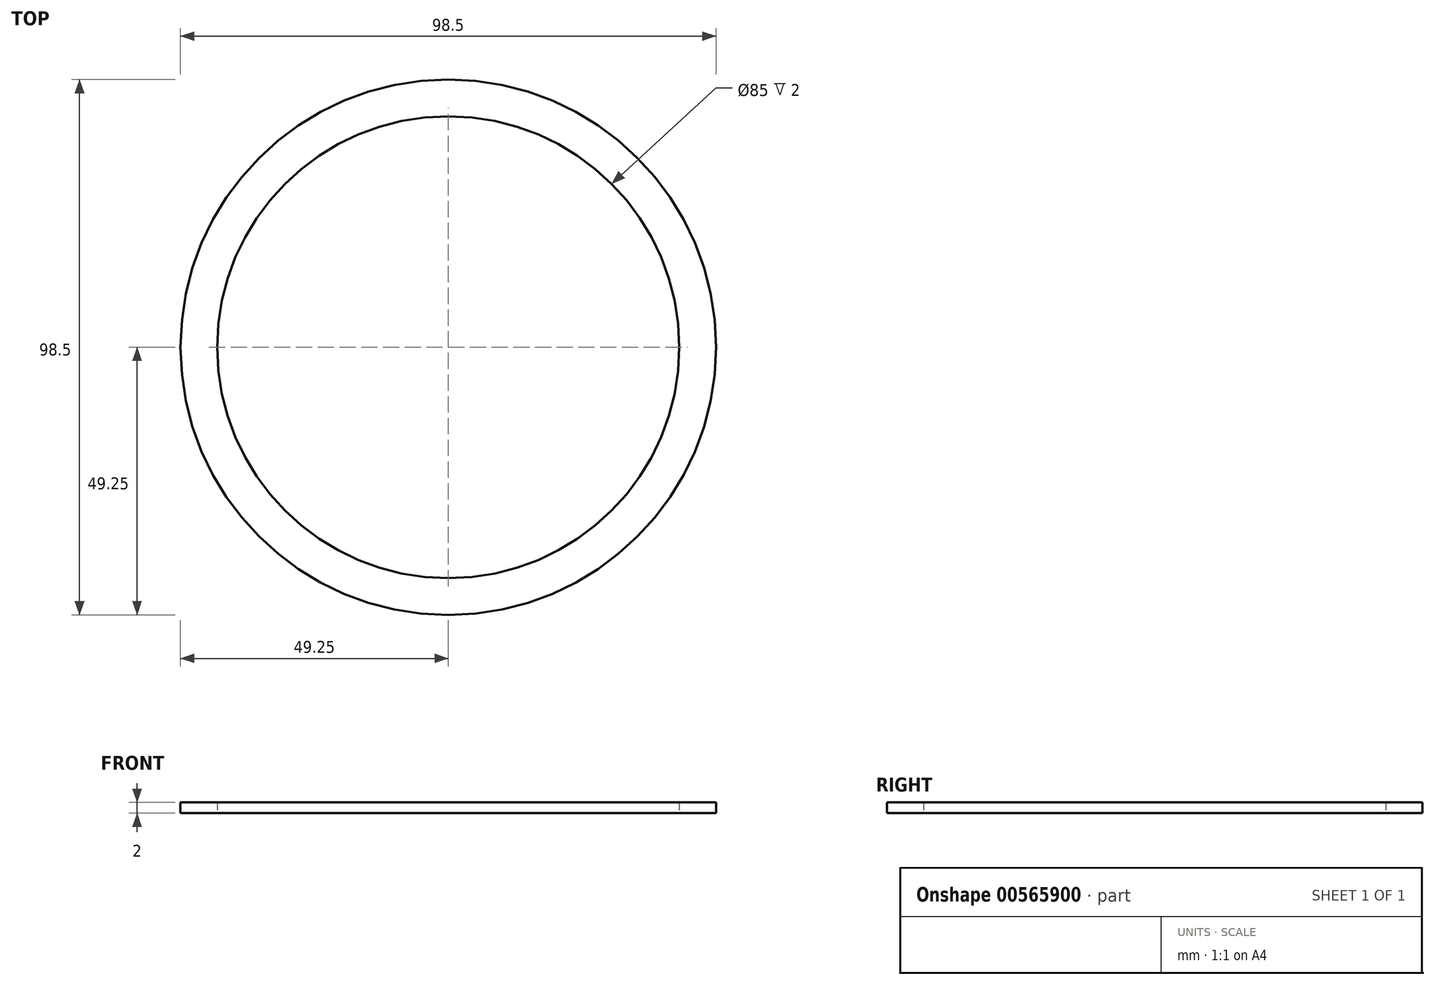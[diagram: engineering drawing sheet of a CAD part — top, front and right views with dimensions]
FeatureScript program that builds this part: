
annotation { "Feature Type Name" : "Feature", "Feature Type Description" : "" }
export const myFeature = defineFeature(function(context is Context, id is Id, definition is map)
    precondition{}
    {
        {
            var Q0;
            Q0=qCreatedBy(makeId("Top.planeOp"),FACE);
            var sketch = newSketch(context, id + "F0", { "sketchPlane" : qUnion([Q0])});
            skCircle(sketch, "E0", {"center": v(0, 0) * mm, "radius": 49.25 * mm});
            skCircle(sketch, "E1", {"center": v(0, 0) * mm, "radius": 42.5 * mm});
            skSolve(sketch);
        }
        {
            var Q0;
            Q0 = qSketchRegion(id + "F0", true);
            extrude(context, id + "F1", {"entities" : qUnion([Q0]), "depth" : 2 * mm, "offsetDistance" : 25 * mm});
        }
    });
